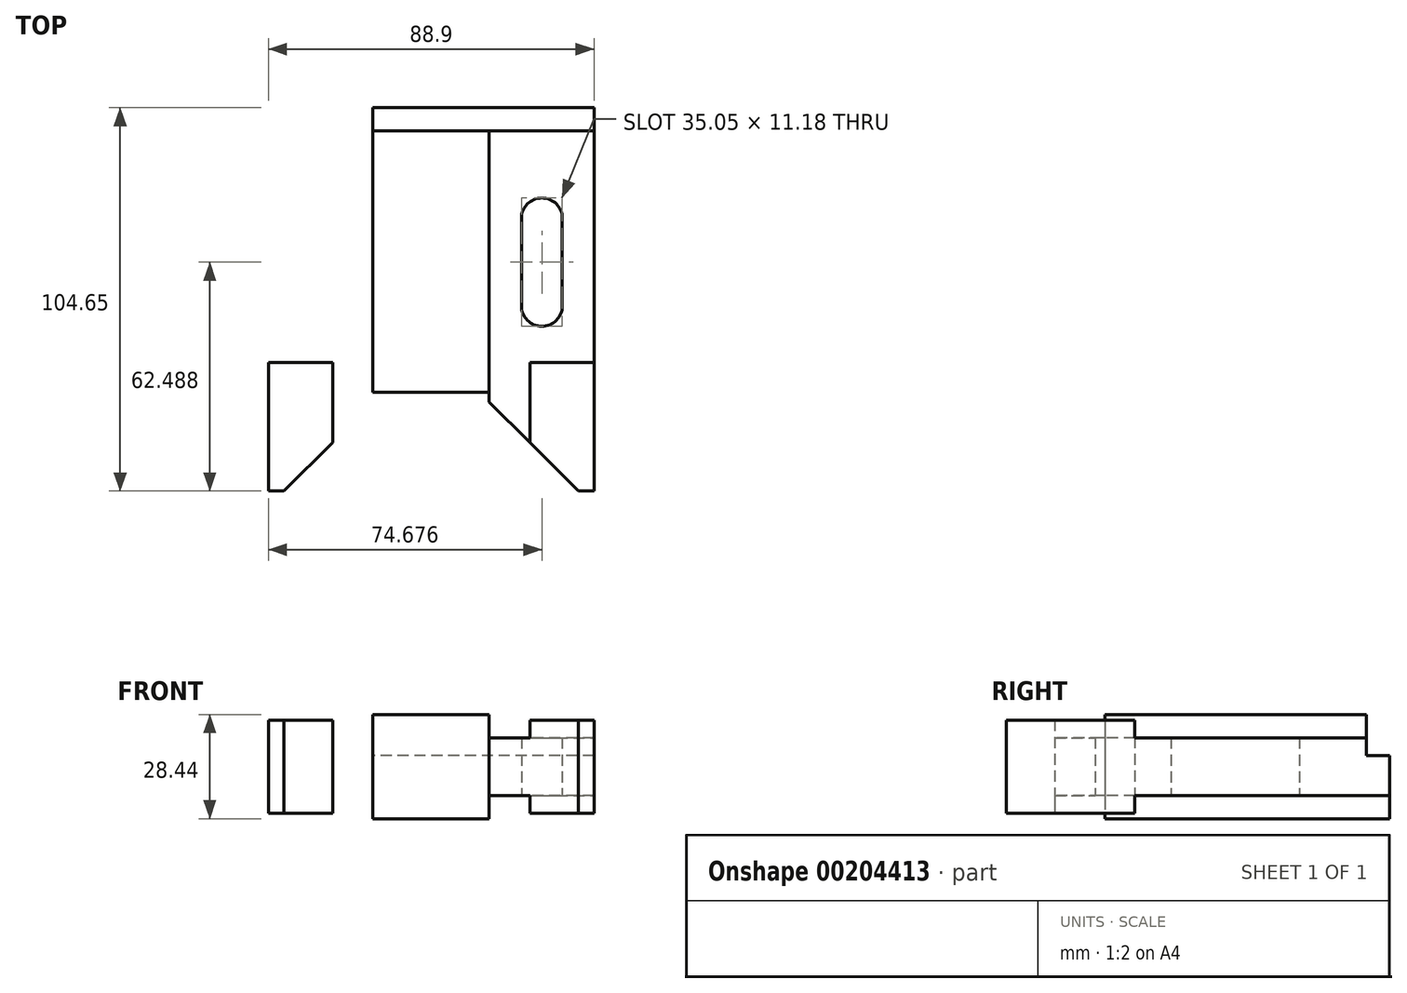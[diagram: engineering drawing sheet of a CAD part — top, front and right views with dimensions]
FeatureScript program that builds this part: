
annotation { "Feature Type Name" : "Feature", "Feature Type Description" : "" }
export const myFeature = defineFeature(function(context is Context, id is Id, definition is map)
    precondition{}
    {
        {
            var Q0;
            Q0=qCreatedBy(makeId("Top.planeOp"),FACE);
            var sketch = newSketch(context, id + "F0", { "sketchPlane" : qUnion([Q0])});
            skLineSegment(sketch, "E0.bottom", {"start": v(-15.88, 38.86) * mm, "end": v(15.88, 38.86) * mm});
            skLineSegment(sketch, "E0.top", {"start": v(-15.88, -38.86) * mm, "end": v(15.88, -38.86) * mm});
            skLineSegment(sketch, "E0.left", {"start": v(-15.87, 38.86) * mm, "end": v(-15.88, -38.86) * mm});
            skLineSegment(sketch, "E0.right", {"start": v(15.88, 38.86) * mm, "end": v(15.87, -38.86) * mm});
            skLineSegment(sketch, "E1", {"start": v(0, 38.86) * mm, "end": v(0, -38.86) * mm, "construction": true});
            skLineSegment(sketch, "E2.bottom", {"start": v(15.88, 38.86) * mm, "end": v(44.45, 38.86) * mm});
            skLineSegment(sketch, "E2.top", {"start": v(15.88, -65.79) * mm, "end": v(44.45, -65.79) * mm});
            skLineSegment(sketch, "E2.left", {"start": v(15.88, 38.86) * mm, "end": v(15.88, -65.79) * mm});
            skLineSegment(sketch, "E2.right", {"start": v(44.45, 38.86) * mm, "end": v(44.45, -65.79) * mm});
            skLineSegment(sketch, "E3.MirrorCS", {"start": v(-44.45, 38.86) * mm, "end": v(-44.45, -65.79) * mm});
            skLineSegment(sketch, "E4.MirrorCS", {"start": v(-15.88, 38.86) * mm, "end": v(-15.88, -65.79) * mm});
            skLineSegment(sketch, "E5.MirrorCS", {"start": v(-15.88, -65.79) * mm, "end": v(-44.45, -65.79) * mm});
            skLineSegment(sketch, "E6.MirrorCS", {"start": v(-15.88, 38.86) * mm, "end": v(-44.45, 38.86) * mm});
            skLineSegment(sketch, "E7.bottom", {"start": v(-35.81, 8.64) * mm, "end": v(-24.64, 8.64) * mm});
            skLineSegment(sketch, "E7.top", {"start": v(-35.81, -15.24) * mm, "end": v(-24.64, -15.24) * mm});
            skLineSegment(sketch, "E7.left", {"start": v(-35.81, 8.64) * mm, "end": v(-35.81, -15.24) * mm});
            skLineSegment(sketch, "E7.right", {"start": v(-24.64, 8.64) * mm, "end": v(-24.64, -15.24) * mm});
            skLineSegment(sketch, "E8", {"start": v(-30.23, 8.64) * mm, "end": v(-30.23, -15.24) * mm, "construction": true});
            skLineSegment(sketch, "E9.MirrorCS", {"start": v(35.81, 8.64) * mm, "end": v(35.81, -15.24) * mm});
            skLineSegment(sketch, "E10.MirrorCS", {"start": v(35.81, 8.64) * mm, "end": v(24.64, 8.64) * mm});
            skLineSegment(sketch, "E11.MirrorCS", {"start": v(35.81, -15.24) * mm, "end": v(24.64, -15.24) * mm});
            skLineSegment(sketch, "E12.MirrorCS", {"start": v(24.64, 8.64) * mm, "end": v(24.64, -15.24) * mm});
            skLineSegment(sketch, "E13.MirrorCS", {"start": v(30.23, 8.64) * mm, "end": v(30.23, -15.24) * mm, "construction": true});
            skCircle(sketch, "E14", {"center": v(0, -86.36) * mm, "radius": 42.93 * mm});
            skPoint(sketch, "E14.second.point", {"position": v(-42.65, -81.5) * mm});
            skPoint(sketch, "E14.third.point", {"position": v(42.65, -81.5) * mm});
            skLineSegment(sketch, "E15.bottom", {"start": v(-44.45, -30.73) * mm, "end": v(-26.92, -30.73) * mm});
            skLineSegment(sketch, "E15.top", {"start": v(-44.45, -65.79) * mm, "end": v(-26.92, -65.79) * mm});
            skLineSegment(sketch, "E15.left", {"start": v(-44.45, -30.73) * mm, "end": v(-44.45, -65.79) * mm});
            skLineSegment(sketch, "E15.right", {"start": v(-26.92, -30.73) * mm, "end": v(-26.92, -65.79) * mm});
            skArc(sketch, "E16", {"start": v(-35.81, 8.64) * mm, "mid": v(-30.23, 14.22) * mm, "end": v(-24.64, 8.64) * mm});
            skArc(sketch, "E17", {"start": v(-35.81, -15.24) * mm, "mid": v(-30.23, -20.83) * mm, "end": v(-24.64, -15.24) * mm});
            skArc(sketch, "E18", {"start": v(24.64, -15.24) * mm, "mid": v(30.23, -20.83) * mm, "end": v(35.81, -15.24) * mm});
            skArc(sketch, "E19", {"start": v(24.64, 8.64) * mm, "mid": v(30.23, 14.22) * mm, "end": v(35.81, 8.64) * mm});
            skLineSegment(sketch, "E20", {"start": v(-40.13, -65.79) * mm, "end": v(-15.88, -41.53) * mm});
            skLineSegment(sketch, "E21", {"start": v(40.13, -65.79) * mm, "end": v(15.88, -41.53) * mm});
            skLineSegment(sketch, "E22.MirrorCS", {"start": v(44.45, -30.73) * mm, "end": v(26.92, -30.73) * mm});
            skLineSegment(sketch, "E23.MirrorCS", {"start": v(26.92, -30.73) * mm, "end": v(26.92, -65.79) * mm});
            skSolve(sketch);
        }
        {
            var Q0;
            {var subQ0=sQuery(id+"F0.wireOp",EDGE,"E0.bottom");Q0=makeQuery(id+"F0.imprint","IMPRINT",FACE,{"disambiguationData":[TD([[makeQuery(id+"F0.imprint","IMPRINT",EDGE,{"derivedFrom":subQ0}),-1.0]])]});}
            extrude(context, id + "F1", {"entities" : qUnion([Q0]), "endBound" : BoundingType.SYMMETRIC, "depth" : 28.45 * mm});
        }
        {
            var Q0;
            Q0=makeQuery(id+"F0.imprint","IMPRINT",FACE,{"disambiguationData":[TD([[makeQuery(id+"F0.imprint","IMPRINT",EDGE,{"derivedFrom":sQuery(id+"F0.wireOp",EDGE,"E3.MirrorCS")}),1.0]])]});
            var Q1;
            {var subQ1=sQuery(id+"F0.wireOp",EDGE,"E2.bottom");Q1=makeQuery(id+"F0.imprint","IMPRINT",FACE,{"disambiguationData":[TD([[makeQuery(id+"F0.imprint","IMPRINT",EDGE,{"derivedFrom":subQ1}),-1.0]])]});}
            extrude(context, id + "F2", {"entities" : qUnion([Q0, Q1]), "operationType" : NewBodyOperationType.ADD, "endBound" : BoundingType.SYMMETRIC, "depth" : 15.75 * mm});
        }
        {
            var Q0;
            Q0=makeQuery(id+"F5.boolean.opBoolean","MERGE",FACE,{"derivedFrom":[makeQuery(id+"F2.opExtrude","SWEPT_FACE",FACE,{"disambiguationData":[OSD([sQuery(id+"F0.wireOp",EDGE,"E3.MirrorCS")])]}),makeQuery(id+"F5.opExtrude","SWEPT_FACE",FACE,{"disambiguationData":[OSD([sQuery(id+"F0.wireOp",EDGE,"E15.left")])]})]});
            var sketch = newSketch(context, id + "F3", { "sketchPlane" : qUnion([Q0])});
            skLineSegment(sketch, "E24.bottom", {"start": v(-38.86, 3.05) * mm, "end": v(-32.51, 3.05) * mm});
            skLineSegment(sketch, "E24.top", {"start": v(-38.86, 17.17) * mm, "end": v(-32.51, 17.17) * mm});
            skLineSegment(sketch, "E24.left", {"start": v(-38.86, 3.05) * mm, "end": v(-38.86, 17.17) * mm});
            skLineSegment(sketch, "E24.right", {"start": v(-32.51, 3.05) * mm, "end": v(-32.51, 17.17) * mm});
            skLineSegment(sketch, "E25.0", {"start": v(-38.86, 7.87) * mm, "end": v(-38.86, -7.87) * mm});
            skSolve(sketch);
        }
        {
            var Q0;
            Q0 = qSketchRegion(id + "F3", true);
            extrude(context, id + "F4", {"entities" : qUnion([Q0]), "operationType" : NewBodyOperationType.REMOVE, "endBound" : BoundingType.THROUGH_ALL, "oppositeDirection" : true, "depth" : 4.83 * mm});
        }
        {
            var Q0;
            {var subQ1=sQuery(id+"F0.wireOp",EDGE,"E15.bottom");Q0=makeQuery(id+"F0.imprint","IMPRINT",FACE,{"disambiguationData":[TD([[makeQuery(id+"F0.imprint","IMPRINT",EDGE,{"derivedFrom":subQ1}),-1.0]])]});}
            var Q1;
            {var subQ3=sQuery(id+"F0.wireOp",EDGE,"E22.MirrorCS");Q1=makeQuery(id+"F0.imprint","IMPRINT",FACE,{"disambiguationData":[TD([[makeQuery(id+"F0.imprint","IMPRINT",EDGE,{"derivedFrom":subQ3}),1.0]])]});}
            extrude(context, id + "F5", {"entities" : qUnion([Q0, Q1]), "operationType" : NewBodyOperationType.ADD, "endBound" : BoundingType.SYMMETRIC, "depth" : 25.4 * mm});
        }
    });
